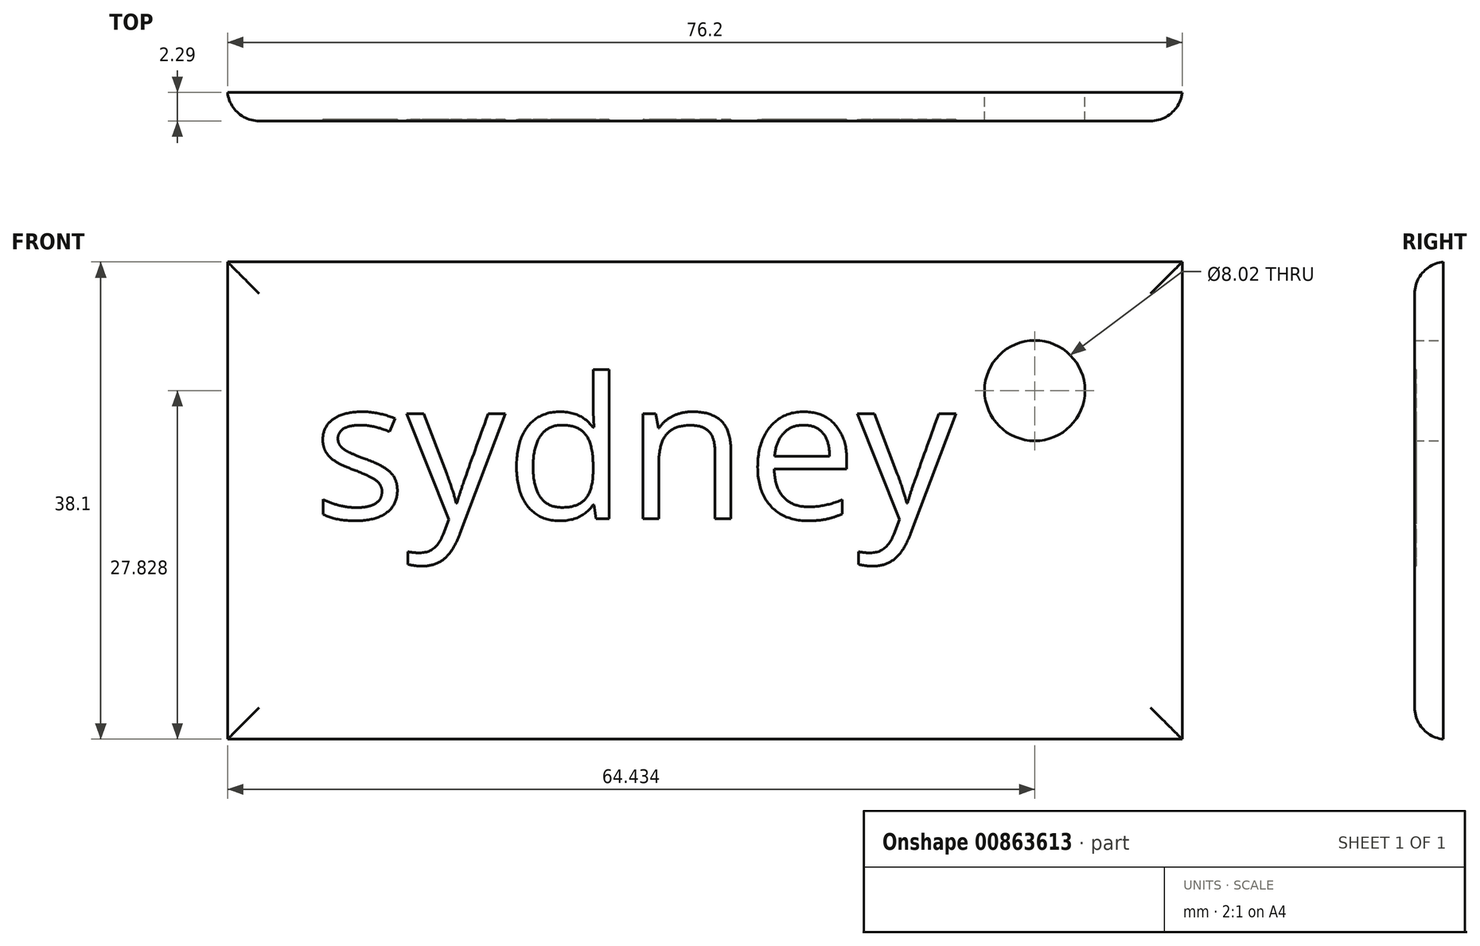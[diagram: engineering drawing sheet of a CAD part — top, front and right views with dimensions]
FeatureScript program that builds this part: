
annotation { "Feature Type Name" : "Feature", "Feature Type Description" : "" }
export const myFeature = defineFeature(function(context is Context, id is Id, definition is map)
    precondition{}
    {
        {
            var Q0;
            Q0=qCreatedBy(makeId("Front.planeOp"),FACE);
            var sketch = newSketch(context, id + "F0", { "sketchPlane" : qUnion([Q0])});
            skLineSegment(sketch, "E0.bottom", {"start": v(-38.1, 19.05) * mm, "end": v(38.1, 19.05) * mm});
            skLineSegment(sketch, "E0.top", {"start": v(-38.1, -19.05) * mm, "end": v(38.1, -19.05) * mm});
            skLineSegment(sketch, "E0.left", {"start": v(-38.1, 19.05) * mm, "end": v(-38.1, -19.05) * mm});
            skLineSegment(sketch, "E0.right", {"start": v(38.1, 19.05) * mm, "end": v(38.1, -19.05) * mm});
            skPoint(sketch, "E0.middle", {"position": v(0, 0) * mm});
            skSolve(sketch);
        }
        {
            var Q0;
            Q0 = qSketchRegion(id + "F0", true);
            extrude(context, id + "F1", {"entities" : qUnion([Q0]), "depth" : 2.3 * mm, "offsetDistance" : 25.4 * mm});
        }
        {
            var Q0;
            Q0=makeQuery(id+"F1.opExtrude","CAP_EDGE",EDGE,{"disambiguationData":[OSD([sQuery(id+"F0.wireOp",EDGE,"E0.left")])],"isStart":false});
            var Q1;
            Q1=makeQuery(id+"F1.opExtrude","CAP_EDGE",EDGE,{"disambiguationData":[OSD([sQuery(id+"F0.wireOp",EDGE,"E0.bottom")])],"isStart":false});
            var Q2;
            Q2=makeQuery(id+"F1.opExtrude","CAP_EDGE",EDGE,{"disambiguationData":[OSD([sQuery(id+"F0.wireOp",EDGE,"E0.right")])],"isStart":false});
            var Q3;
            Q3=makeQuery(id+"F1.opExtrude","CAP_EDGE",EDGE,{"disambiguationData":[OSD([sQuery(id+"F0.wireOp",EDGE,"E0.top")])],"isStart":false});
            fillet(context, id + "F2", {"entities" : qUnion([Q0, Q1, Q2, Q3]), "radius" : 2.54 * mm, "tangentPropagation" : true, "allowEdgeOverflow" : false});
        }
        {
            var Q0;
            Q0=qCreatedBy(makeId("Front.planeOp"),FACE);
            var sketch = newSketch(context, id + "F3", { "sketchPlane" : qUnion([Q0])});
            skCircle(sketch, "E1", {"center": v(28.06, 10.22) * mm, "radius": 3.28 * mm});
            skSolve(sketch);
        }
        {
            var Q0;
            Q0 = qSketchRegion(id + "F3", true);
            extrude(context, id + "F4", {"entities" : qUnion([Q0]), "operationType" : NewBodyOperationType.REMOVE, "oppositeDirection" : true, "depth" : 25.4 * mm, "offsetDistance" : 25.4 * mm});
        }
        {
            var Q0;
            Q0=qCreatedBy(makeId("Front.planeOp"),FACE);
            var sketch = newSketch(context, id + "F5", { "sketchPlane" : qUnion([Q0])});
            skCircle(sketch, "E2", {"center": v(27.49, 10.22) * mm, "radius": 3.84 * mm});
            skSolve(sketch);
        }
        {
            var Q0;
            Q0 = qSketchRegion(id + "F5", true);
            extrude(context, id + "F6", {"entities" : qUnion([Q0]), "operationType" : NewBodyOperationType.REMOVE, "endBound" : BoundingType.THROUGH_ALL, "oppositeDirection" : true, "depth" : 25.4 * mm, "offsetDistance" : 25.4 * mm});
        }
        {
            var Q0;
            Q0=makeQuery(id+"F1.opExtrude","CAP_FACE",FACE,{"disambiguationData":[OSD([sQuery(id+"F0.wireOp",EDGE,"E0.bottom"),sQuery(id+"F0.wireOp",EDGE,"E0.top"),sQuery(id+"F0.wireOp",EDGE,"E0.left"),sQuery(id+"F0.wireOp",EDGE,"E0.right")])],"isStart":false});
            var sketch = newSketch(context, id + "F7", { "sketchPlane" : qUnion([Q0])});
            skText(sketch, "E3", { "text": "sydney", "fontName": "OpenSans-Regular.ttf"});
            const initialGuessF7  = {"E3": [-0.03131, -0.00146, 1, 0, 0.0113]};
            skSetInitialGuess(sketch, initialGuessF7);
            skSolve(sketch);
        }
        {
            var Q0;
            Q0 = qSketchRegion(id + "F7", true);
            extrude(context, id + "F8", {"entities" : qUnion([Q0]), "operationType" : NewBodyOperationType.REMOVE, "oppositeDirection" : true, "depth" : 0.13 * mm, "offsetDistance" : 25.4 * mm});
        }
        {
            var Q0;
            Q0=qCreatedBy(makeId("Front.planeOp"),FACE);
            var sketch = newSketch(context, id + "F9", { "sketchPlane" : qUnion([Q0])});
            skCircle(sketch, "E4", {"center": v(26.33, 8.78) * mm, "radius": 4 * mm});
            skSolve(sketch);
        }
        {
            var Q0;
            Q0 = qSketchRegion(id + "F9", true);
            extrude(context, id + "F10", {"entities" : qUnion([Q0]), "operationType" : NewBodyOperationType.REMOVE, "endBound" : BoundingType.THROUGH_ALL, "depth" : 25.4 * mm, "offsetDistance" : 25.4 * mm});
        }
    });
